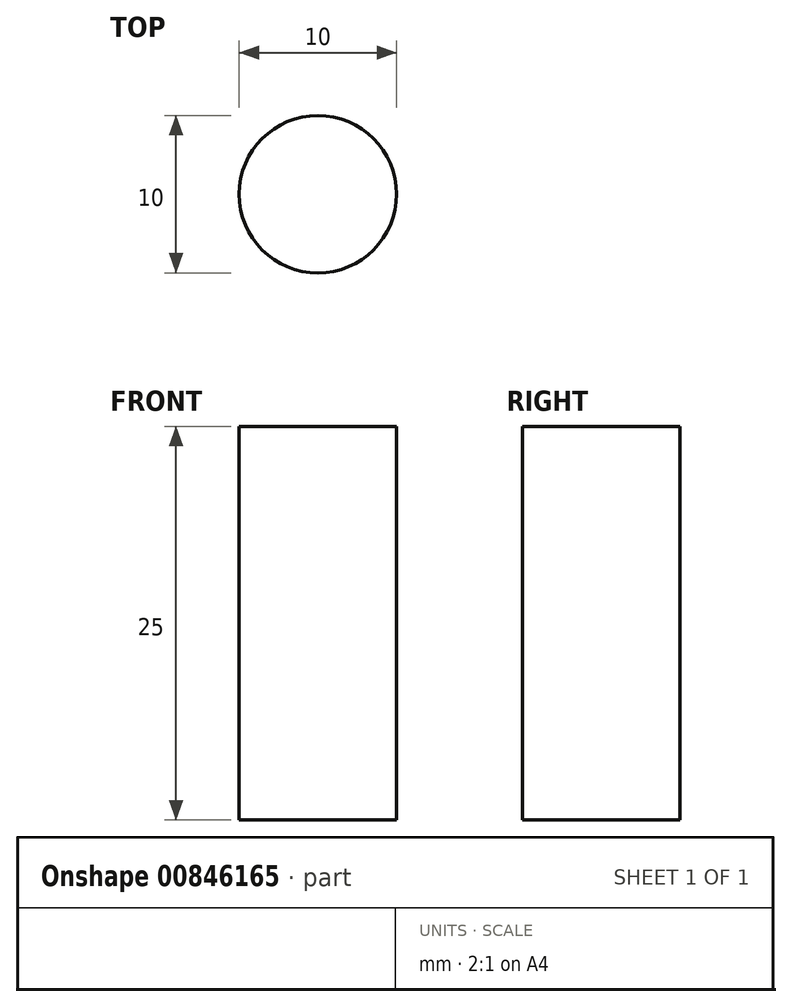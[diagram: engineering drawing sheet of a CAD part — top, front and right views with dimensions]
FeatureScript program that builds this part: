
annotation { "Feature Type Name" : "Feature", "Feature Type Description" : "" }
export const myFeature = defineFeature(function(context is Context, id is Id, definition is map)
    precondition{}
    {
        {
            var Q0;
            Q0=qCreatedBy(makeId("Top.planeOp"),FACE);
            var sketch = newSketch(context, id + "F0", { "sketchPlane" : qUnion([Q0])});
            skCircle(sketch, "E0", {"center": v(0, 0) * mm, "radius": 5 * mm});
            skSolve(sketch);
        }
        {
            var Q0;
            Q0=makeQuery(id+"F0.imprint","IMPRINT",FACE,{"disambiguationData":[TD([[makeQuery(id+"F0.imprint","IMPRINT",EDGE,{"derivedFrom":sQuery(id+"F0.wireOp",EDGE,"E0")}),1.0]])]});
            extrude(context, id + "F1", {"entities" : qUnion([Q0]), "depth" : 25 * mm, "offsetDistance" : 25 * mm});
        }
    });
